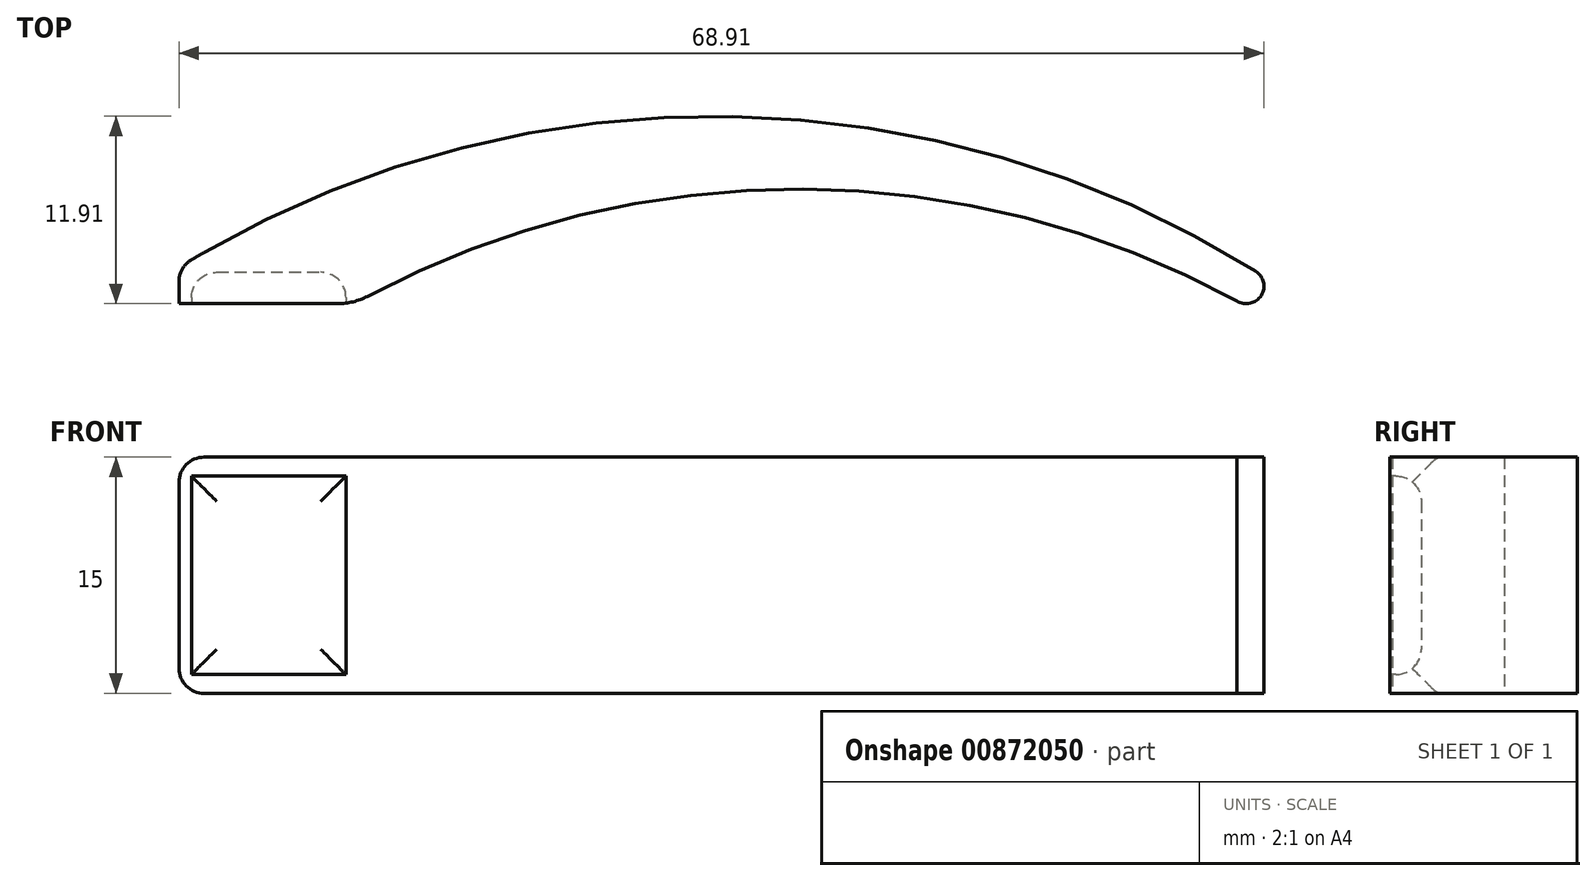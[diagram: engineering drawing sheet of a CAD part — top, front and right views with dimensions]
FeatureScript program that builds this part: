
annotation { "Feature Type Name" : "Feature", "Feature Type Description" : "" }
export const myFeature = defineFeature(function(context is Context, id is Id, definition is map)
    precondition{}
    {
        {
            var Q0;
            Q0=qCreatedBy(makeId("Top.planeOp"),FACE);
            var sketch = newSketch(context, id + "F0", { "sketchPlane" : qUnion([Q0])});
            skArc(sketch, "E0", {"start": v(34.39, 2.07) * mm, "mid": v(0.23, 11.9) * mm, "end": v(-34, 2.3) * mm});
            skArc(sketch, "E1", {"start": v(33.2, 0.17) * mm, "mid": v(5.13, 7.28) * mm, "end": v(-22.89, 0) * mm});
            skLineSegment(sketch, "E2", {"start": v(-34, 0) * mm, "end": v(-22.89, 0) * mm});
            skPoint(sketch, "E3.orphan", {"position": v(37.5, 0) * mm});
            skLineSegment(sketch, "E4", {"start": v(0, -53.1) * mm, "end": v(34.39, 2.07) * mm, "construction": true});
            skArc(sketch, "E5", {"start": v(33.2, 0.17) * mm, "mid": v(34.74, 0.53) * mm, "end": v(34.39, 2.07) * mm});
            skPoint(sketch, "E6.orphan", {"position": v(-37.5, 0) * mm});
            skLineSegment(sketch, "E7", {"start": v(-34, 0) * mm, "end": v(-34, 2.3) * mm});
            skSolve(sketch);
        }
        {
            var Q0;
            Q0 = qSketchRegion(id + "F0", true);
            extrude(context, id + "F1", {"entities" : qUnion([Q0]), "endBound" : BoundingType.SYMMETRIC, "depth" : 15 * mm, "offsetDistance" : 25 * mm});
        }
        {
            var Q0;
            Q0=qCreatedBy(makeId("Front.planeOp"),FACE);
            var sketch = newSketch(context, id + "F2", { "sketchPlane" : qUnion([Q0])});
            skLineSegment(sketch, "E8.bottom", {"start": v(-33.2, 6.3) * mm, "end": v(-23.39, 6.3) * mm});
            skLineSegment(sketch, "E8.top", {"start": v(-33.2, -6.3) * mm, "end": v(-23.39, -6.3) * mm});
            skLineSegment(sketch, "E8.left", {"start": v(-23.39, -6.3) * mm, "end": v(-23.39, 6.3) * mm});
            skLineSegment(sketch, "E8.right", {"start": v(-33.2, 6.3) * mm, "end": v(-33.2, -6.3) * mm});
            skPoint(sketch, "E8.middle", {"position": v(-28.3, 0) * mm});
            skSolve(sketch);
        }
        {
            var Q0;
            Q0 = qSketchRegion(id + "F2", true);
            extrude(context, id + "F3", {"entities" : qUnion([Q0]), "operationType" : NewBodyOperationType.REMOVE, "oppositeDirection" : true, "depth" : 2 * mm, "offsetDistance" : 25 * mm});
        }
        {
            var Q0;
            Q0=makeQuery(id+"F3.boolean.opBoolean","COPY",FACE,{"derivedFrom":makeQuery(id+"F3.opExtrude","CAP_FACE",FACE,{"disambiguationData":[OSD([sQuery(id+"F2.wireOp",EDGE,"E8.bottom"),sQuery(id+"F2.wireOp",EDGE,"E8.top"),sQuery(id+"F2.wireOp",EDGE,"E8.left"),sQuery(id+"F2.wireOp",EDGE,"E8.right")])],"isStart":false})});
            var Q1;
            Q1=makeQuery(id+"F1.opExtrude","SWEPT_EDGE",EDGE,{"disambiguationData":[OSD([sQuery(id+"F0.wireOp",EDGE,"E0"),sQuery(id+"F0.wireOp",EDGE,"E7")])]});
            var Q2;
            Q2=makeQuery(id+"F1.opExtrude","CAP_EDGE",EDGE,{"disambiguationData":[OSD([sQuery(id+"F0.wireOp",EDGE,"E7")])],"isStart":false});
            var Q3;
            Q3=makeQuery(id+"F1.opExtrude","CAP_EDGE",EDGE,{"disambiguationData":[OSD([sQuery(id+"F0.wireOp",EDGE,"E7")])],"isStart":true});
            fillet(context, id + "F4", {"entities" : qUnion([Q0, Q1, Q2, Q3]), "radius" : 1.6 * mm, "tangentPropagation" : true, "allowEdgeOverflow" : false});
        }
        {
            var Q0;
            Q0=makeQuery(id+"F1.opExtrude","SWEPT_EDGE",EDGE,{"disambiguationData":[OSD([sQuery(id+"F0.wireOp",EDGE,"E1"),sQuery(id+"F0.wireOp",EDGE,"E2")])]});
            fillet(context, id + "F5", {"entities" : qUnion([Q0]), "radius" : 4 * mm, "tangentPropagation" : true, "allowEdgeOverflow" : false});
        }
    });
